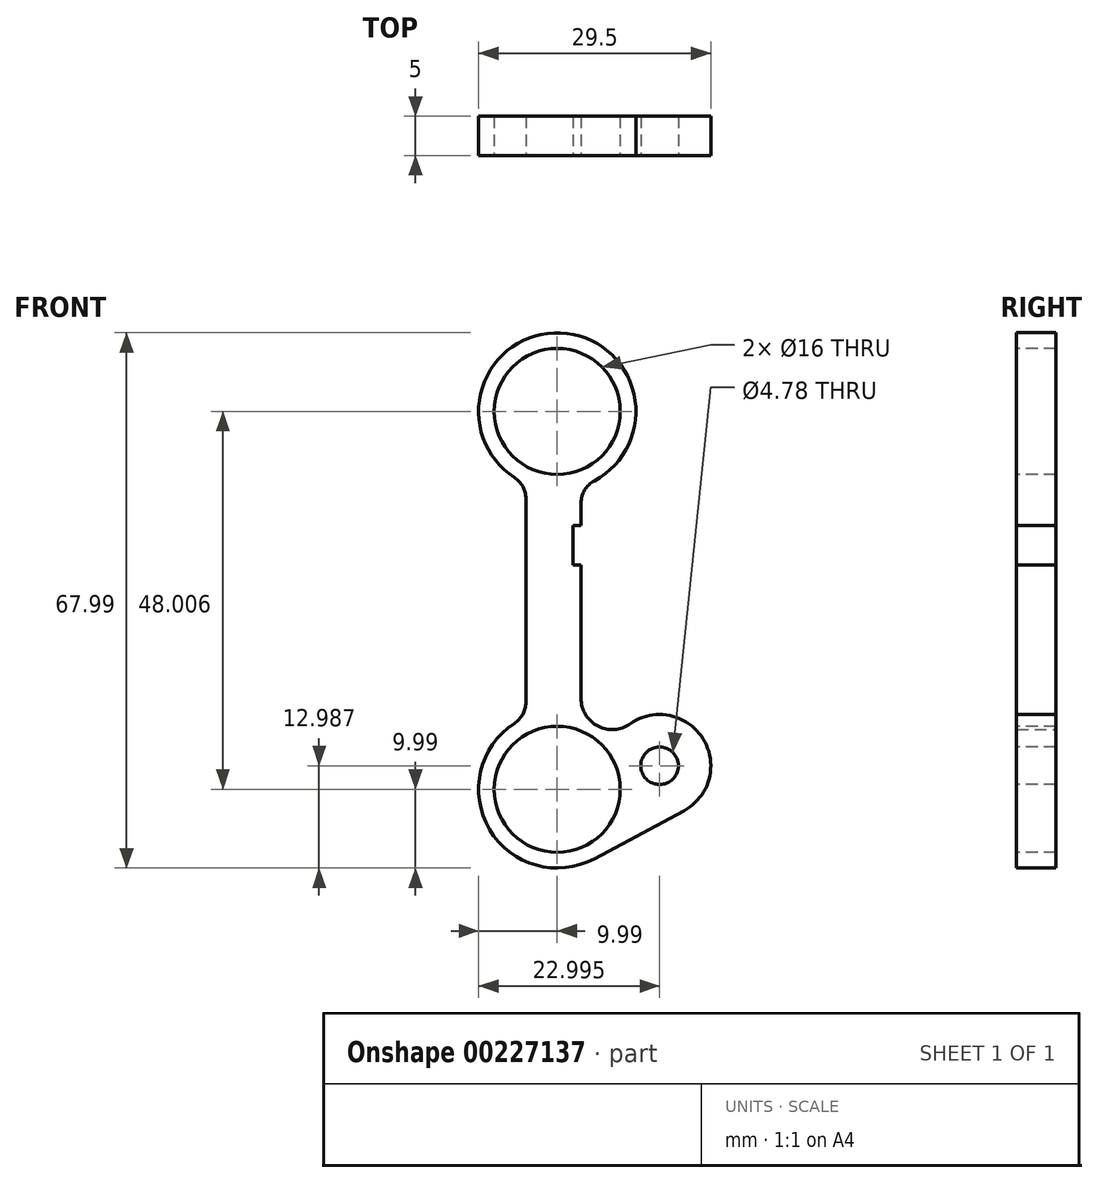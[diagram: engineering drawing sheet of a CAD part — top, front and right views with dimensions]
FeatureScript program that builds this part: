
annotation { "Feature Type Name" : "Feature", "Feature Type Description" : "" }
export const myFeature = defineFeature(function(context is Context, id is Id, definition is map)
    precondition{}
    {
        {
            var Q0;
            Q0=qCreatedBy(makeId("Front.planeOp"),FACE);
            var sketch = newSketch(context, id + "F0", { "sketchPlane" : qUnion([Q0])});
            skArc(sketch, "E0", {"start": v(-3.99, 9.16) * mm, "mid": v(-9, -4.36) * mm, "end": v(4.72, -8.81) * mm});
            skCircle(sketch, "E1", {"center": v(0, 48) * mm, "radius": 10 * mm});
            skLineSegment(sketch, "E2", {"start": v(-3.99, 38.84) * mm, "end": v(-3.99, 9.16) * mm});
            skLineSegment(sketch, "E3", {"start": v(3.02, 38.48) * mm, "end": v(3.02, 11.57) * mm});
            skArc(sketch, "E4", {"start": v(16.07, -2.74) * mm, "mid": v(18.54, 6.4) * mm, "end": v(9.27, 8.32) * mm});
            skLineSegment(sketch, "E5", {"start": v(4.72, -8.81) * mm, "end": v(16.07, -2.74) * mm});
            skLineSegment(sketch, "E6", {"start": v(9.27, 8.32) * mm, "end": v(9.27, 8.32) * mm});
            skArc(sketch, "E7", {"start": v(3.02, 11.57) * mm, "mid": v(5.16, 8.05) * mm, "end": v(9.27, 8.32) * mm});
            skSolve(sketch);
        }
        {
            var Q0;
            {var subQ0=sQuery(id+"F0.wireOp",EDGE,"E1");var subQ1=makeQuery(id+"F0.imprint","INTERSECT",VERTEX,{"derivedFrom":[subQ0,sQuery(id+"F0.wireOp",EDGE,"E2")]});Q0=makeQuery(id+"F0.imprint","IMPRINT",FACE,{"disambiguationData":[TD([[makeQuery(id+"F0.imprint","IMPRINT",EDGE,{"disambiguationData":[TD([[subQ1,-1.0]])],"derivedFrom":subQ0}),1.0]])]});}
            var Q1;
            {var subQ0=sQuery(id+"F0.wireOp",EDGE,"E2");Q1=makeQuery(id+"F0.imprint","IMPRINT",FACE,{"disambiguationData":[TD([[makeQuery(id+"F0.imprint","IMPRINT",EDGE,{"derivedFrom":subQ0}),1.0]])]});}
            var Q2;
            {var subQ0=sQuery(id+"F0.wireOp",EDGE,"E0");var subQ1=makeQuery(id+"F0.imprint","INTERSECT",VERTEX,{"derivedFrom":[subQ0,sQuery(id+"F0.wireOp",EDGE,"E2")]});Q2=makeQuery(id+"F0.imprint","IMPRINT",FACE,{"disambiguationData":[TD([[makeQuery(id+"F0.imprint","IMPRINT",EDGE,{"disambiguationData":[TD([[subQ1,1.0]])],"derivedFrom":subQ0}),1.0]])]});}
            extrude(context, id + "F1", {"entities" : qUnion([Q0, Q1, Q2]), "depth" : 5 * mm});
        }
        {
            var Q0;
            Q0=makeQuery(id+"F1.opExtrude","SWEPT_EDGE",EDGE,{"disambiguationData":[OSD([sQuery(id+"F0.wireOp",EDGE,"E1"),sQuery(id+"F0.wireOp",EDGE,"E2")])]});
            var Q1;
            Q1=makeQuery(id+"F1.opExtrude","SWEPT_EDGE",EDGE,{"disambiguationData":[OSD([sQuery(id+"F0.wireOp",EDGE,"E1"),sQuery(id+"F0.wireOp",EDGE,"E3")])]});
            var Q2;
            Q2=makeQuery(id+"F1.opExtrude","SWEPT_EDGE",EDGE,{"disambiguationData":[OSD([sQuery(id+"F0.wireOp",EDGE,"E0"),sQuery(id+"F0.wireOp",EDGE,"E3")])]});
            var Q3;
            Q3=makeQuery(id+"F1.opExtrude","SWEPT_EDGE",EDGE,{"disambiguationData":[OSD([sQuery(id+"F0.wireOp",EDGE,"E0"),sQuery(id+"F0.wireOp",EDGE,"E2")])]});
            fillet(context, id + "F2", {"entities" : qUnion([Q0, Q1, Q2, Q3]), "radius" : 3.17 * mm, "tangentPropagation" : true, "allowEdgeOverflow" : false});
        }
        {
            var Q0;
            Q0=makeQuery(id+"F1.opExtrude","CAP_FACE",FACE,{"disambiguationData":[OSD([sQuery(id+"F0.wireOp",EDGE,"E0"),sQuery(id+"F0.wireOp",EDGE,"E1"),sQuery(id+"F0.wireOp",EDGE,"E2"),sQuery(id+"F0.wireOp",EDGE,"E3"),sQuery(id+"F0.wireOp",EDGE,"E4"),sQuery(id+"F0.wireOp",EDGE,"E5"),sQuery(id+"F0.wireOp",EDGE,"011a694e-866c-4b7e-a2bb-fac31ed5cf10.filletArc")])],"isStart":false});
            var sketch = newSketch(context, id + "F3", { "sketchPlane" : qUnion([Q0])});
            skCircle(sketch, "E8", {"center": v(0, 0) * mm, "radius": 8 * mm});
            skCircle(sketch, "E9", {"center": v(0, 48) * mm, "radius": 8 * mm});
            skSolve(sketch);
        }
        {
            var Q0;
            Q0=makeQuery(id+"F3.imprint","IMPRINT",FACE,{"disambiguationData":[TD([[makeQuery(id+"F3.imprint","IMPRINT",EDGE,{"derivedFrom":sQuery(id+"F3.wireOp",EDGE,"E9")}),1.0]])]});
            var Q1;
            Q1=makeQuery(id+"F3.imprint","IMPRINT",FACE,{"disambiguationData":[TD([[makeQuery(id+"F3.imprint","IMPRINT",EDGE,{"derivedFrom":sQuery(id+"F3.wireOp",EDGE,"E8")}),1.0]])]});
            extrude(context, id + "F4", {"entities" : qUnion([Q0, Q1]), "operationType" : NewBodyOperationType.REMOVE, "oppositeDirection" : true, "depth" : 5 * mm});
        }
        {
            var Q0;
            Q0=makeQuery(id+"F1.opExtrude","CAP_FACE",FACE,{"disambiguationData":[OSD([sQuery(id+"F0.wireOp",EDGE,"E0"),sQuery(id+"F0.wireOp",EDGE,"E1"),sQuery(id+"F0.wireOp",EDGE,"E2"),sQuery(id+"F0.wireOp",EDGE,"E3"),sQuery(id+"F0.wireOp",EDGE,"E4"),sQuery(id+"F0.wireOp",EDGE,"E5"),sQuery(id+"F0.wireOp",EDGE,"011a694e-866c-4b7e-a2bb-fac31ed5cf10.filletArc")])],"isStart":false});
            var sketch = newSketch(context, id + "F5", { "sketchPlane" : qUnion([Q0])});
            skLineSegment(sketch, "E10", {"start": v(0, 48) * mm, "end": v(-28.62, 48) * mm});
            skLineSegment(sketch, "E11.bottom", {"start": v(3.02, 33.5) * mm, "end": v(2, 33.5) * mm});
            skLineSegment(sketch, "E11.top", {"start": v(3.02, 28.5) * mm, "end": v(2, 28.5) * mm});
            skLineSegment(sketch, "E11.left", {"start": v(3.02, 33.5) * mm, "end": v(3.02, 28.5) * mm});
            skLineSegment(sketch, "E11.right", {"start": v(2, 33.5) * mm, "end": v(2, 28.5) * mm});
            skSolve(sketch);
        }
        {
            var Q0;
            Q0=makeQuery(id+"F5.imprint","IMPRINT",FACE,{"disambiguationData":[TD([[makeQuery(id+"F5.imprint","IMPRINT",EDGE,{"derivedFrom":sQuery(id+"F5.wireOp",EDGE,"E11.bottom")}),1.0]])]});
            extrude(context, id + "F6", {"entities" : qUnion([Q0]), "operationType" : NewBodyOperationType.REMOVE, "oppositeDirection" : true, "depth" : 5 * mm});
        }
        {
            var Q0;
            Q0=makeQuery(id+"F1.opExtrude","CAP_FACE",FACE,{"disambiguationData":[OSD([sQuery(id+"F0.wireOp",EDGE,"E0"),sQuery(id+"F0.wireOp",EDGE,"E1"),sQuery(id+"F0.wireOp",EDGE,"E2"),sQuery(id+"F0.wireOp",EDGE,"E3"),sQuery(id+"F0.wireOp",EDGE,"E4"),sQuery(id+"F0.wireOp",EDGE,"E5"),sQuery(id+"F0.wireOp",EDGE,"E7")])],"isStart":false});
            var sketch = newSketch(context, id + "F7", { "sketchPlane" : qUnion([Q0])});
            skCircle(sketch, "E12", {"center": v(13, 3) * mm, "radius": 2.39 * mm});
            skSolve(sketch);
        }
        {
            var Q0;
            Q0=makeQuery(id+"F7.imprint","IMPRINT",FACE,{"disambiguationData":[TD([[makeQuery(id+"F7.imprint","IMPRINT",EDGE,{"derivedFrom":sQuery(id+"F7.wireOp",EDGE,"E12")}),1.0]])]});
            extrude(context, id + "F8", {"entities" : qUnion([Q0]), "operationType" : NewBodyOperationType.REMOVE, "oppositeDirection" : true, "depth" : 5 * mm});
        }
    });
